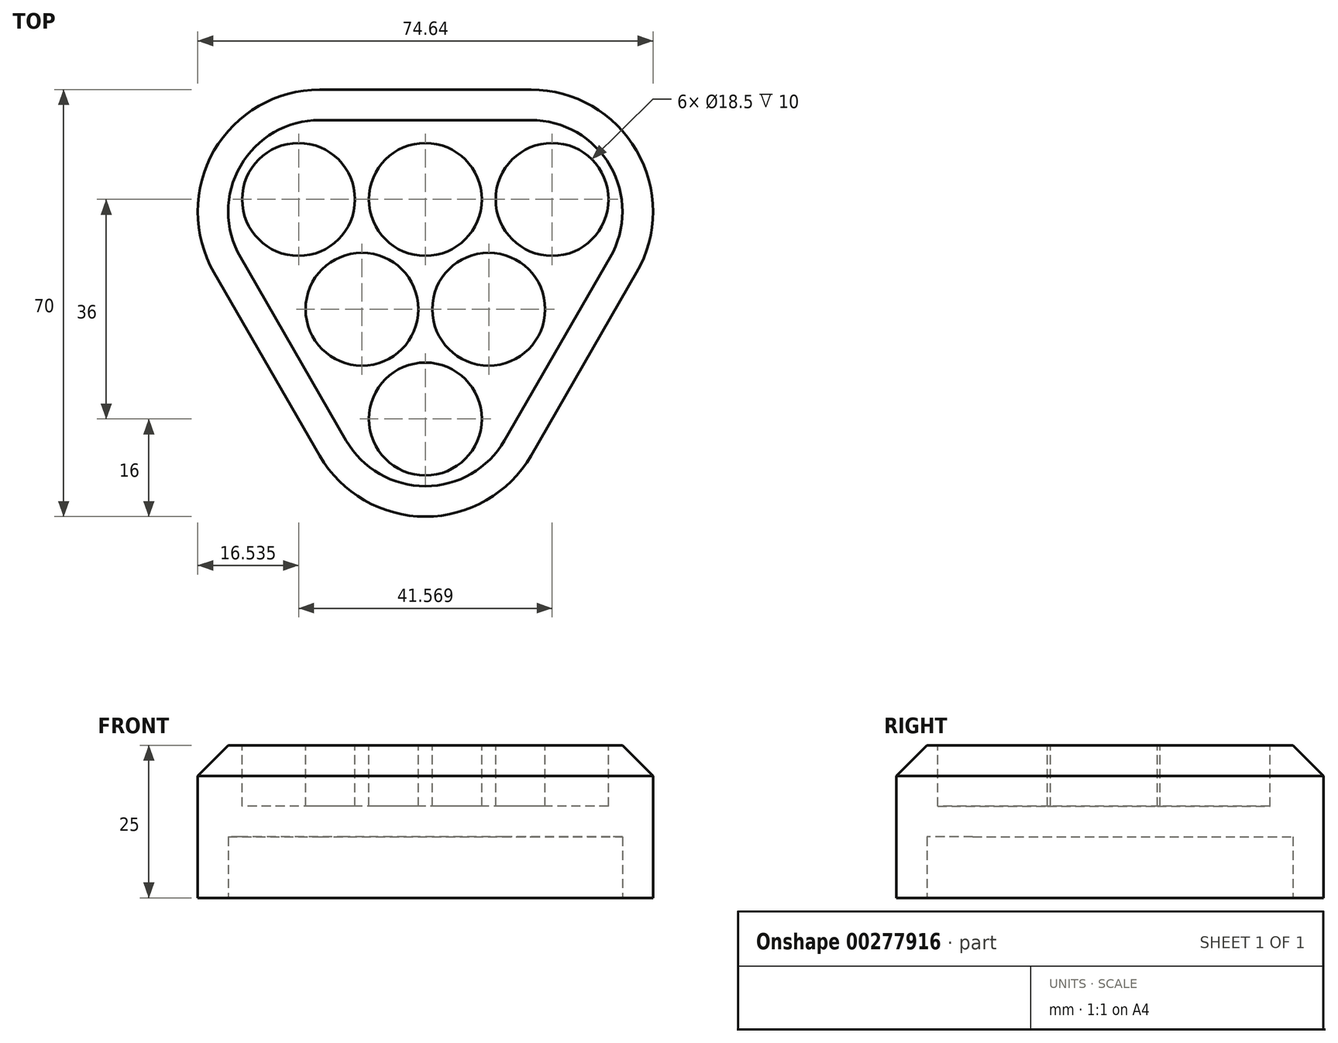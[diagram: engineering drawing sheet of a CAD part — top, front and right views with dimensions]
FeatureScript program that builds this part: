
annotation { "Feature Type Name" : "Feature", "Feature Type Description" : "" }
export const myFeature = defineFeature(function(context is Context, id is Id, definition is map)
    precondition{}
    {
        {
            var Q0;
            Q0=qCreatedBy(makeId("Top.planeOp"),FACE);
            var sketch = newSketch(context, id + "F0", { "sketchPlane" : qUnion([Q0])});
            skCircle(sketch, "E0.cCircle", {"center": v(0, 0) * mm, "radius": 30 * mm, "construction": true});
            skLineSegment(sketch, "E0.0", {"start": v(-17.32, 30) * mm, "end": v(17.32, 30) * mm});
            skLineSegment(sketch, "E0.1", {"start": v(34.64, 0) * mm, "end": v(17.32, -30) * mm});
            skLineSegment(sketch, "E0.2", {"start": v(-17.32, -30) * mm, "end": v(-34.64, 0) * mm});
            skPoint(sketch, "E0.0.midPoint", {"position": v(0, 30) * mm});
            skLineSegment(sketch, "E1", {"start": v(0, 0) * mm, "end": v(-51.96, 30) * mm, "construction": true});
            skCircle(sketch, "E2", {"center": v(-17.32, 10) * mm, "radius": 12.5 * mm, "construction": true});
            skCircle(sketch, "E3.1.0", {"center": v(0, -20) * mm, "radius": 12.5 * mm, "construction": true});
            skCircle(sketch, "E3.2.0", {"center": v(17.32, 10) * mm, "radius": 12.5 * mm, "construction": true});
            skLineSegment(sketch, "E4", {"start": v(-17.32, 10) * mm, "end": v(-17.32, 30) * mm, "construction": true});
            skPoint(sketch, "E5.visualSharp", {"position": v(-51.96, 30) * mm});
            skArc(sketch, "E5.filletArc", {"start": v(-17.32, 30) * mm, "mid": v(-34.64, 20) * mm, "end": v(-34.64, 0) * mm});
            skPoint(sketch, "E6.visualSharp", {"position": v(0, -60) * mm});
            skArc(sketch, "E6.filletArc", {"start": v(-17.32, -30) * mm, "mid": v(0, -40) * mm, "end": v(17.32, -30) * mm});
            skPoint(sketch, "E7.visualSharp", {"position": v(51.96, 30) * mm});
            skArc(sketch, "E7.filletArc", {"start": v(34.64, 0) * mm, "mid": v(34.64, 20) * mm, "end": v(17.32, 30) * mm});
            skSolve(sketch);
        }
        {
            var Q0;
            Q0=qSketchRegion(id+"F0",true);
            extrude(context, id + "F1", {"entities" : qUnion([Q0]), "depth" : 25 * mm});
        }
        {
            var Q0;
            Q0=makeQuery(id+"F1.opExtrude","CAP_FACE",FACE,{"disambiguationData":[OSD([sQuery(id+"F0.wireOp",EDGE,"E0.0"),sQuery(id+"F0.wireOp",EDGE,"E0.1"),sQuery(id+"F0.wireOp",EDGE,"E0.2"),sQuery(id+"F0.wireOp",EDGE,"E5.filletArc"),sQuery(id+"F0.wireOp",EDGE,"E6.filletArc"),sQuery(id+"F0.wireOp",EDGE,"E7.filletArc")])],"isStart":false});
            var sketch = newSketch(context, id + "F2", { "sketchPlane" : qUnion([Q0])});
            skLineSegment(sketch, "E8", {"start": v(0, 0) * mm, "end": v(-34.64, 20) * mm, "construction": true});
            skCircle(sketch, "E9", {"center": v(-20.78, 12) * mm, "radius": 9.25 * mm});
            skCircle(sketch, "E10.1.0", {"center": v(0, -24) * mm, "radius": 9.25 * mm});
            skCircle(sketch, "E10.2.0", {"center": v(20.78, 12) * mm, "radius": 9.25 * mm});
            skPoint(sketch, "E10.center", {"position": v(0, 0) * mm});
            skLineSegment(sketch, "E11", {"start": v(-20.78, 12) * mm, "end": v(20.78, 12) * mm, "construction": true});
            skCircle(sketch, "E12", {"center": v(0, 12) * mm, "radius": 9.25 * mm});
            skCircle(sketch, "E13.1.0", {"center": v(-10.4, -6) * mm, "radius": 9.25 * mm});
            skCircle(sketch, "E13.2.0", {"center": v(10.4, -6) * mm, "radius": 9.25 * mm});
            skSolve(sketch);
        }
        {
            var Q0;
            Q0=qSketchRegion(id+"F2",true);
            extrude(context, id + "F3", {"entities" : qUnion([Q0]), "operationType" : NewBodyOperationType.REMOVE, "oppositeDirection" : true, "depth" : 10 * mm});
        }
        {
            var Q0;
            Q0=makeQuery(id+"F1.opExtrude","CAP_EDGE",EDGE,{"disambiguationData":[OSD([sQuery(id+"F0.wireOp",EDGE,"E0.1")])],"isStart":false});
            chamfer(context, id + "F4", {"entities" : qUnion([Q0]), "width" : 5 * mm, "tangentPropagation" : true});
        }
        {
            var Q0;
            Q0=makeQuery(id+"F1.opExtrude","CAP_FACE",FACE,{"disambiguationData":[OSD([sQuery(id+"F0.wireOp",EDGE,"E0.0"),sQuery(id+"F0.wireOp",EDGE,"E0.1"),sQuery(id+"F0.wireOp",EDGE,"E0.2"),sQuery(id+"F0.wireOp",EDGE,"E5.filletArc"),sQuery(id+"F0.wireOp",EDGE,"E6.filletArc"),sQuery(id+"F0.wireOp",EDGE,"E7.filletArc")])],"isStart":true});
            var sketch = newSketch(context, id + "F5", { "sketchPlane" : qUnion([Q0])});
            skArc(sketch, "E14.0", {"start": v(-13, 27.5) * mm, "mid": v(0, 35) * mm, "end": v(13, 27.5) * mm});
            skArc(sketch, "E14.1", {"start": v(-17.32, -25) * mm, "mid": v(-30.31, -17.5) * mm, "end": v(-30.31, -2.5) * mm});
            skLineSegment(sketch, "E14.2", {"start": v(-17.32, -25) * mm, "end": v(17.32, -25) * mm});
            skLineSegment(sketch, "E14.3", {"start": v(-13, 27.5) * mm, "end": v(-30.31, -2.5) * mm});
            skArc(sketch, "E14.4", {"start": v(30.31, -2.5) * mm, "mid": v(30.31, -17.5) * mm, "end": v(17.32, -25) * mm});
            skLineSegment(sketch, "E14.5", {"start": v(30.31, -2.5) * mm, "end": v(13, 27.5) * mm});
            skSolve(sketch);
        }
        {
            var Q0;
            Q0 = qSketchRegion(id + "F5", true);
            extrude(context, id + "F6", {"entities" : qUnion([Q0]), "operationType" : NewBodyOperationType.REMOVE, "oppositeDirection" : true, "depth" : 10 * mm});
        }
    });
